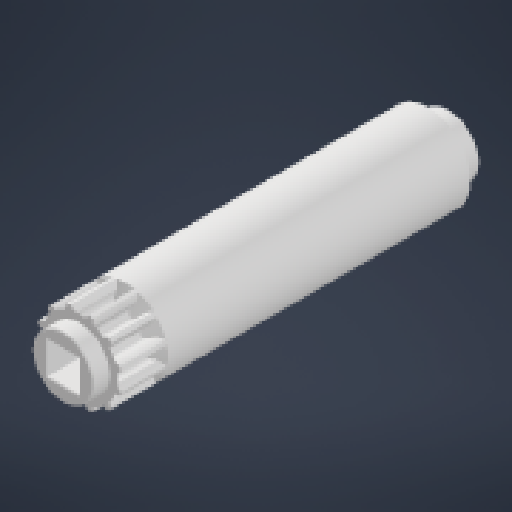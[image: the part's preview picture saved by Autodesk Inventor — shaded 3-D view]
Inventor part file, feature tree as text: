
AUTODESK INVENTOR PART (.ipt)
format: ipt  version: 2024.1 (Build 281209000, 209)  size: 669,184 bytes
history: native  units: in
note: dims shown in document units (in); Inventor stores cm internally (conversion verified against a paired STEP export)
features: extrude x10, sketch x7, projected_geometry x6, chamfer x5, reference x3, other x3, revolve x2, pattern_circular x1
ambient origin geometry x8: Origin, YZ Plane, XZ Plane, XY Plane, X Axis, Y Axis, Z Axis, Center Point
bodies: Solid1 (feature_tree)
feature tree (37):
  extrude  "Extrusion1"  TaperAngle=0.0deg  [1 undecoded]
  extrude  "Extrusion2"  Depth=4.7244in TaperAngle=360.0deg
  pattern_circular  "Circular Pattern1"  Angle=45.0deg  [1 undecoded]
  sketch  "Sketch2"  dims[d0=0.73in d1=0.0in]
  extrude  "Extrusion3"  TaperAngle=30.0deg  [1 undecoded]
  extrude  "Extrusion4"  TaperAngle=90.0deg  [1 undecoded]
  chamfer  "Chamfer1"  Angle=30.0deg  [1 undecoded]
  sketch  "Sketch3"  dims[d2=0.0in d3=0.0in d4=4.7244in d5=360.0deg]
  revolve  "Revolution1"  [1 undecoded]
  revolve  "Revolution2"  Angle=90.0deg
  extrude  "Extrusion5"  Depth=0.1675in TaperAngle=0.0deg
  extrude  "Extrusion6"  Depth=0.1675in TaperAngle=0.0deg
  chamfer  "Chamfer2"  Distance=0.3in
  sketch  "Sketch6"  dims[d9=0.16in]
  extrude  "Extrusion7"  Depth=0.1675in TaperAngle=0.0deg
  chamfer  "Chamfer3"  Distance=0.005in Angle=45.0deg
  extrude  "Extrusion8"  Depth=0.103in TaperAngle=0.0deg
  extrude  "Extrusion9"  Depth=0.1675in TaperAngle=45.0deg
  chamfer  "Chamfer4"  Distance=0.1875in
  extrude  "Extrusion10"  Depth=0.1675in
  chamfer  "Chamfer5"  Distance=0.1675in
  projected_geometry  "Projected Loop1"
  reference  "Reference1"
  reference  "Reference2"
  reference  "Reference3"
  projected_geometry  "Projected Loop2"
  projected_geometry  "Projected Loop3"
  sketch  "Sketch4"  dims[d7=0.25in]
  sketch  "Sketch5"  dims[d8=0.16in]
  projected_geometry  "Projected Loop4"
  projected_geometry  "Projected Loop5"
  projected_geometry  "Projected Loop6"
  sketch  "Sketch7"  dims[d10=0.0825in d11=0.0in]
  sketch  "Sketch8"  dims[d12=0.1875in d13=0.0in d14=0.005in d15=0.125in d16=45.0deg d17=30.0deg d18=90.0deg d19=30.0deg d20=0.085in d21=90.0deg d22=0.99in d23=0.0in d24=0.5051in d25=0.0in d26=0.3in d27=1.0115in d28=0.0in d29=0.005in d30=0.125in d31=45.0deg d32=0.103in d33=0.0in d34=0.005in d35=0.125in d36=45.0deg d37=0.1875in d38=0.0in d39=0.12in d40=0.1675in d41=0.0in d42=0.005in d43=0.125in d44=45.0deg d45=0.1675in d46=0.0in d47=0.005in d48=0.125in d49=45.0deg]
  other  "<userpath>\Documents\School\FallCAD\Bio\Bio.iam"
  other  "Bio.iam"
  other  "Bio50t:1"
note: 6 required parameter values undecoded (feature->parameter linkage not recoverable at this tier; creation-order binding heuristic only, values carry confidence <= 0.55)